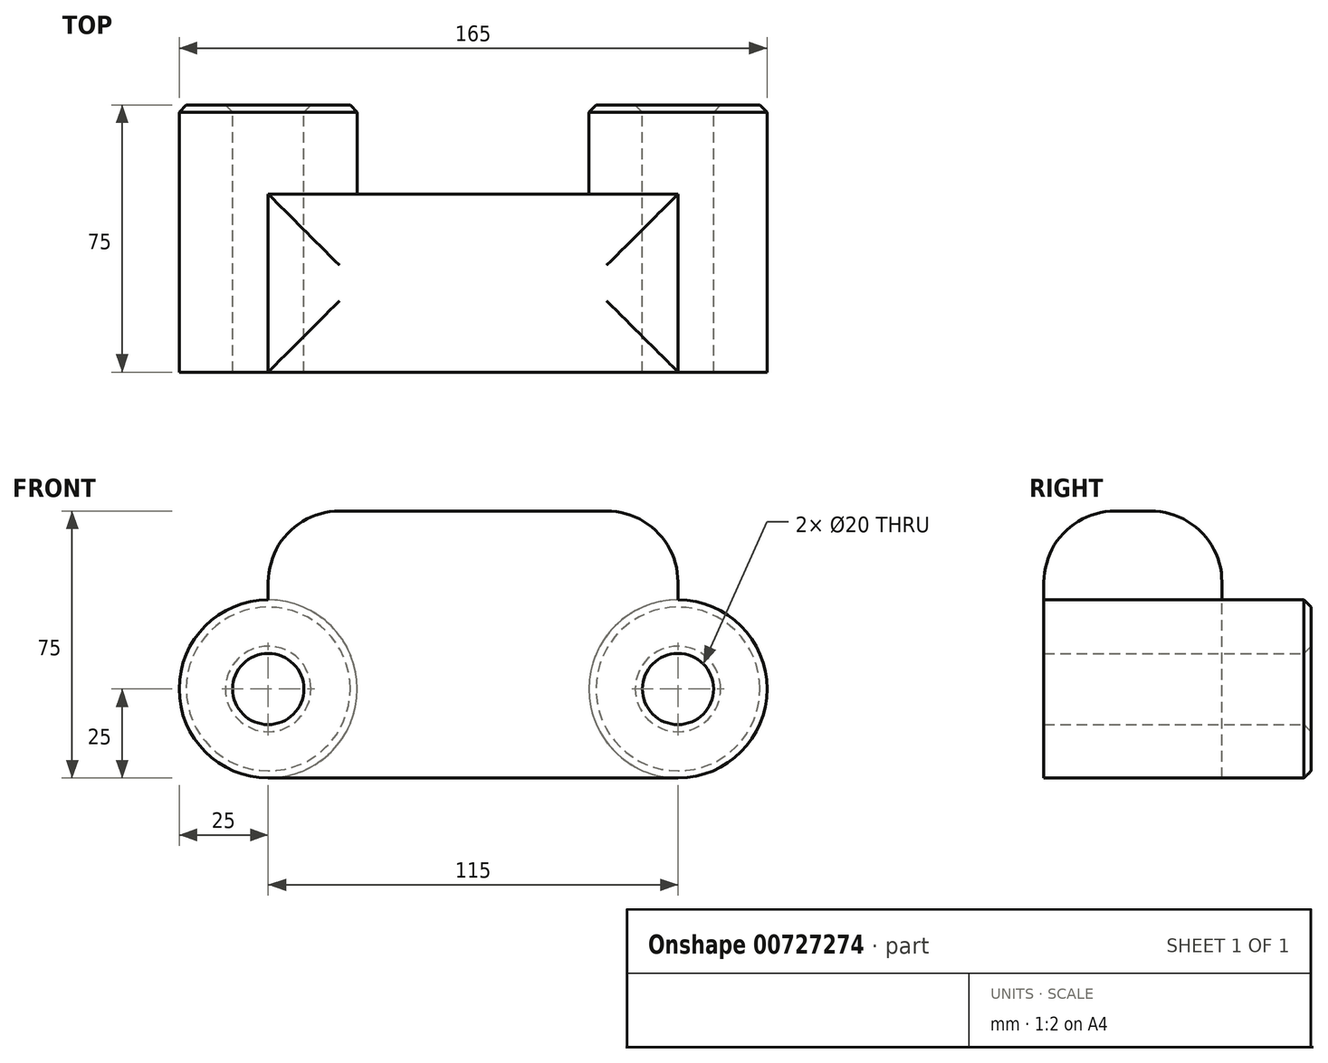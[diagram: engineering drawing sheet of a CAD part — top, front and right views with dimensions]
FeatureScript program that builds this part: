
annotation { "Feature Type Name" : "Feature", "Feature Type Description" : "" }
export const myFeature = defineFeature(function(context is Context, id is Id, definition is map)
    precondition{}
    {
        {
            var Q0;
            Q0=qCreatedBy(makeId("Front.planeOp"),FACE);
            var sketch = newSketch(context, id + "F0", { "sketchPlane" : qUnion([Q0])});
            skCircle(sketch, "E0", {"center": v(0, 0) * mm, "radius": 25 * mm});
            skCircle(sketch, "E1", {"center": v(115, 0) * mm, "radius": 25 * mm});
            skLineSegment(sketch, "E2", {"start": v(0, 25) * mm, "end": v(115, 25) * mm});
            skLineSegment(sketch, "E3", {"start": v(0, -25) * mm, "end": v(115, -25) * mm});
            skCircle(sketch, "E4", {"center": v(0, 0) * mm, "radius": 10 * mm});
            skCircle(sketch, "E5", {"center": v(115, 0) * mm, "radius": 10 * mm});
            skSolve(sketch);
        }
        {
            var Q0;
            Q0 = qSketchRegion(id + "F0", true);
            extrude(context, id + "F1", {"entities" : qUnion([Q0]), "depth" : 50 * mm, "offsetDistance" : 25 * mm});
        }
        {
            var Q0;
            Q0=makeQuery(id+"F0.imprint","IMPRINT",FACE,{"disambiguationData":[TD([[makeQuery(id+"F0.imprint","IMPRINT",EDGE,{"derivedFrom":sQuery(id+"F0.wireOp",EDGE,"E5")}),-1.0]])]});
            var Q1;
            Q1=makeQuery(id+"F0.imprint","IMPRINT",FACE,{"disambiguationData":[TD([[makeQuery(id+"F0.imprint","IMPRINT",EDGE,{"derivedFrom":sQuery(id+"F0.wireOp",EDGE,"E4")}),-1.0]])]});
            extrude(context, id + "F2", {"entities" : qUnion([Q0, Q1]), "operationType" : NewBodyOperationType.ADD, "oppositeDirection" : true, "depth" : 25 * mm, "offsetDistance" : 25 * mm});
        }
        {
            var Q0;
            Q0=makeQuery(id+"F2.opExtrude","CAP_EDGE",EDGE,{"disambiguationData":[OSD([sQuery(id+"F0.wireOp",EDGE,"E5")])],"isStart":false});
            var Q1;
            Q1=makeQuery(id+"F2.opExtrude","CAP_EDGE",EDGE,{"disambiguationData":[OSD([sQuery(id+"F0.wireOp",EDGE,"E1")])],"isStart":false});
            var Q2;
            Q2=makeQuery(id+"F2.opExtrude","CAP_EDGE",EDGE,{"disambiguationData":[OSD([sQuery(id+"F0.wireOp",EDGE,"E4")])],"isStart":false});
            var Q3;
            Q3=makeQuery(id+"F2.opExtrude","CAP_EDGE",EDGE,{"disambiguationData":[OSD([sQuery(id+"F0.wireOp",EDGE,"E0")])],"isStart":false});
            chamfer(context, id + "F3", {"entities" : qUnion([Q0, Q1, Q2, Q3]), "width" : 2 * mm, "tangentPropagation" : true});
        }
        {
            var Q0;
            Q0=makeQuery(id+"F1.opExtrude","SWEPT_FACE",FACE,{"disambiguationData":[OSD([sQuery(id+"F0.wireOp",EDGE,"E2")])]});
            extrude(context, id + "F4", {"entities" : qUnion([Q0]), "operationType" : NewBodyOperationType.ADD, "depth" : 25 * mm, "offsetDistance" : 25 * mm});
        }
        {
            var Q0;
            Q0=makeQuery(id+"F4.opExtrude","CAP_EDGE",EDGE,{"disambiguationData":[OSD([sQuery(id+"F0.wireOp",EDGE,"E1"),sQuery(id+"F0.wireOp",EDGE,"E2")])],"isStart":false});
            var Q1;
            {var subQ0=sQuery(id+"F0.wireOp",EDGE,"E2");Q1=makeQuery(id+"F4.opExtrude","CAP_EDGE",EDGE,{"disambiguationData":[OSD([subQ0]),TDD([makeQuery(id+"F1.opExtrude","CAP_EDGE",EDGE,{"disambiguationData":[OSD([subQ0])],"isStart":true})])],"isStart":false});}
            var Q2;
            {var subQ0=sQuery(id+"F0.wireOp",EDGE,"E2");Q2=makeQuery(id+"F4.opExtrude","CAP_EDGE",EDGE,{"disambiguationData":[OSD([subQ0]),TDD([makeQuery(id+"F1.opExtrude","CAP_EDGE",EDGE,{"disambiguationData":[OSD([subQ0])],"isStart":false})])],"isStart":false});}
            var Q3;
            Q3=makeQuery(id+"F4.opExtrude","CAP_EDGE",EDGE,{"disambiguationData":[OSD([sQuery(id+"F0.wireOp",EDGE,"E0"),sQuery(id+"F0.wireOp",EDGE,"E2")])],"isStart":false});
            fillet(context, id + "F5", {"entities" : qUnion([Q0, Q1, Q2, Q3]), "radius" : 20 * mm, "tangentPropagation" : true, "allowEdgeOverflow" : false});
        }
    });
